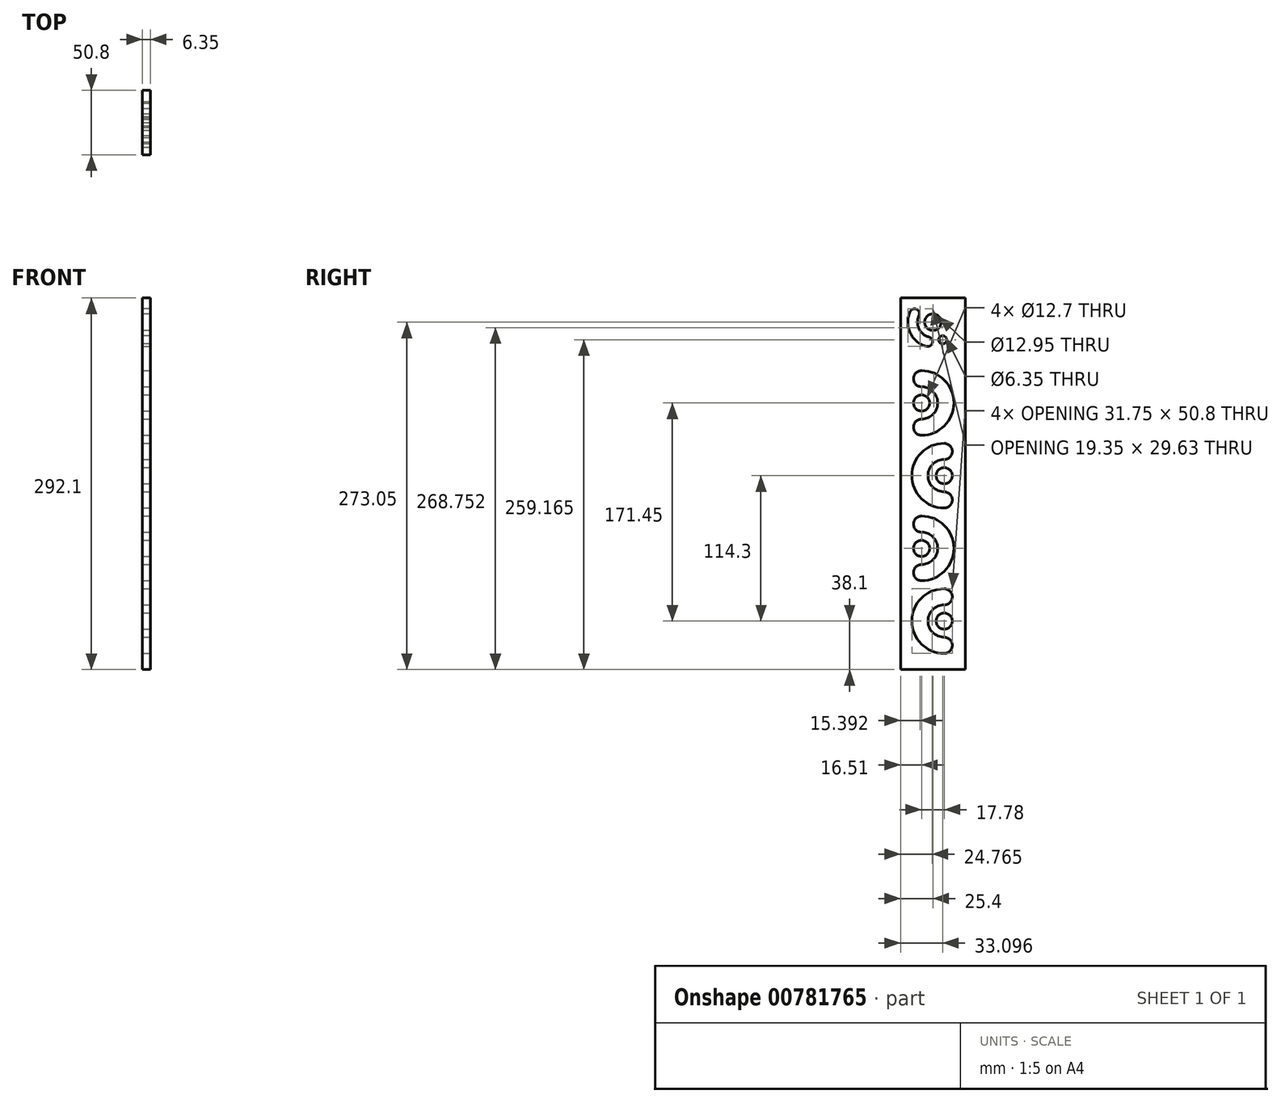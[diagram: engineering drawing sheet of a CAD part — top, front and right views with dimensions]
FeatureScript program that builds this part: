
annotation { "Feature Type Name" : "Feature", "Feature Type Description" : "" }
export const myFeature = defineFeature(function(context is Context, id is Id, definition is map)
    precondition{}
    {
        {
            var Q0;
            Q0=qCreatedBy(makeId("Top.planeOp"),FACE);
            var sketch = newSketch(context, id + "F0", { "sketchPlane" : qUnion([Q0])});
            skLineSegment(sketch, "E0.bottom", {"start": v(31.75, -31.75) * mm, "end": v(-31.75, -31.75) * mm});
            skLineSegment(sketch, "E0.top", {"start": v(31.75, 31.75) * mm, "end": v(-31.75, 31.75) * mm});
            skLineSegment(sketch, "E0.left", {"start": v(31.75, -31.75) * mm, "end": v(31.75, 31.75) * mm});
            skLineSegment(sketch, "E0.right", {"start": v(-31.75, -31.75) * mm, "end": v(-31.75, 31.75) * mm});
            skPoint(sketch, "E0.middle", {"position": v(0, 0) * mm});
            skLineSegment(sketch, "E1.bottom", {"start": v(25.4, -25.4) * mm, "end": v(-25.4, -25.4) * mm});
            skLineSegment(sketch, "E1.top", {"start": v(25.4, 25.4) * mm, "end": v(-25.4, 25.4) * mm});
            skLineSegment(sketch, "E1.left", {"start": v(25.4, -25.4) * mm, "end": v(25.4, 25.4) * mm});
            skLineSegment(sketch, "E1.right", {"start": v(-25.4, -25.4) * mm, "end": v(-25.4, 25.4) * mm});
            skSolve(sketch);
        }
        {
            var Q0;
            Q0=makeQuery(id+"F0.imprint","IMPRINT",FACE,{"disambiguationData":[TD([[makeQuery(id+"F0.imprint","IMPRINT",EDGE,{"derivedFrom":sQuery(id+"F0.wireOp",EDGE,"E0.bottom")}),-1.0]])]});
            extrude(context, id + "F1", {"entities" : qUnion([Q0]), "endBound" : BoundingType.SYMMETRIC, "depth" : 330.2 * mm, "offsetDistance" : 25.4 * mm});
        }
        {
            var Q0;
            Q0=makeQuery(id+"F1.opExtrude","SWEPT_FACE",FACE,{"disambiguationData":[OSD([sQuery(id+"F0.wireOp",EDGE,"E0.right")])]});
            var sketch = newSketch(context, id + "F2", { "sketchPlane" : qUnion([Q0])});
            skSolve(sketch);
        }
        {
            var Q0;
            Q0=makeQuery(id+"F1.opExtrude","SWEPT_FACE",FACE,{"disambiguationData":[OSD([sQuery(id+"F0.wireOp",EDGE,"E0.left")])]});
            var sketch = newSketch(context, id + "F3", { "sketchPlane" : qUnion([Q0])});
            skLineSegment(sketch, "E2.0", {"start": v(-31.75, 165.1) * mm, "end": v(31.75, 165.1) * mm, "construction": true});
            skLineSegment(sketch, "E2.1", {"start": v(-31.75, 165.1) * mm, "end": v(-31.75, -165.1) * mm, "construction": true});
            skLineSegment(sketch, "E2.2", {"start": v(31.75, 165.1) * mm, "end": v(31.75, -165.1) * mm, "construction": true});
            skLineSegment(sketch, "E2.3", {"start": v(-31.75, -165.1) * mm, "end": v(31.75, -165.1) * mm, "construction": true});
            skCircle(sketch, "E3", {"center": v(0, 146.05) * mm, "radius": 6.48 * mm});
            skArc(sketch, "E4", {"start": v(17.84, 137.73) * mm, "mid": v(19.5, 143.31) * mm, "end": v(19.44, 149.13) * mm});
            skArc(sketch, "E5", {"start": v(10.93, 140.95) * mm, "mid": v(11.95, 144.37) * mm, "end": v(11.92, 147.94) * mm});
            skLineSegment(sketch, "E6", {"start": v(0, 146.05) * mm, "end": v(19.44, 149.13) * mm, "construction": true});
            skLineSegment(sketch, "E7", {"start": v(0, 146.05) * mm, "end": v(9.54, 128.83) * mm, "construction": true});
            skLineSegment(sketch, "E8", {"start": v(0, 146.05) * mm, "end": v(24.19, 134.77) * mm, "construction": true});
            skCircle(sketch, "E9", {"center": v(0, 146.05) * mm, "radius": 15.88 * mm, "construction": true});
            skArc(sketch, "E10", {"start": v(11.92, 147.94) * mm, "mid": v(15.08, 152.3) * mm, "end": v(19.44, 149.13) * mm});
            skArc(sketch, "E11.MirrorCS", {"start": v(6.21, 135.7) * mm, "mid": v(4.91, 130.48) * mm, "end": v(10.14, 129.18) * mm});
            skArc(sketch, "E12.MirrorCS", {"start": v(10.93, 140.95) * mm, "mid": v(8.97, 137.98) * mm, "end": v(6.21, 135.7) * mm});
            skArc(sketch, "E13.MirrorCS", {"start": v(17.84, 137.73) * mm, "mid": v(14.63, 132.88) * mm, "end": v(10.14, 129.18) * mm});
            skLineSegment(sketch, "E14", {"start": v(0, 146.05) * mm, "end": v(-19.11, 146.05) * mm, "construction": true});
            skLineSegment(sketch, "E15", {"start": v(0, 146.05) * mm, "end": v(0, 119.4) * mm, "construction": true});
            skArc(sketch, "E16.MirrorCS", {"start": v(-6.21, 135.7) * mm, "mid": v(-4.91, 130.48) * mm, "end": v(-10.14, 129.18) * mm});
            skArc(sketch, "E17.MirrorCS", {"start": v(-17.84, 137.73) * mm, "mid": v(-14.63, 132.88) * mm, "end": v(-10.14, 129.18) * mm});
            skArc(sketch, "E18.MirrorCS", {"start": v(-17.84, 137.73) * mm, "mid": v(-19.5, 143.31) * mm, "end": v(-19.44, 149.13) * mm});
            skArc(sketch, "E19.MirrorCS", {"start": v(-11.92, 147.94) * mm, "mid": v(-15.08, 152.3) * mm, "end": v(-19.44, 149.13) * mm});
            skArc(sketch, "E20.MirrorCS", {"start": v(-10.93, 140.95) * mm, "mid": v(-11.95, 144.37) * mm, "end": v(-11.92, 147.94) * mm});
            skArc(sketch, "E21.MirrorCS", {"start": v(-10.93, 140.95) * mm, "mid": v(-8.97, 137.98) * mm, "end": v(-6.21, 135.7) * mm});
            skSolve(sketch);
        }
        {
            var Q0;
            Q0=makeQuery(id+"F3.imprint","IMPRINT",FACE,{"disambiguationData":[TD([[makeQuery(id+"F3.imprint","IMPRINT",EDGE,{"derivedFrom":sQuery(id+"F3.wireOp",EDGE,"E3")}),1.0]])]});
            var Q1;
            Q1=makeQuery(id+"F3.imprint","IMPRINT",FACE,{"disambiguationData":[TD([[makeQuery(id+"F3.imprint","IMPRINT",EDGE,{"derivedFrom":sQuery(id+"F3.wireOp",EDGE,"E4")}),1.0]])]});
            var Q2;
            Q2=makeQuery(id+"F3.imprint","IMPRINT",FACE,{"disambiguationData":[TD([[makeQuery(id+"F3.imprint","IMPRINT",EDGE,{"derivedFrom":sQuery(id+"F3.wireOp",EDGE,"E16.MirrorCS")}),-1.0]])]});
            extrude(context, id + "F4", {"entities" : qUnion([Q0, Q1, Q2]), "operationType" : NewBodyOperationType.REMOVE, "oppositeDirection" : true, "depth" : 25.4 * mm, "offsetDistance" : 25.4 * mm});
        }
        {
            var Q0;
            {var subQ0=sQuery(id+"F0.wireOp",EDGE,"E0.right");Q0=makeQuery(id+"F2.imprint","IMPRINT",FACE,{"disambiguationData":[TD([[makeQuery(id+"F2.imprint","IMPRINT",EDGE,{"derivedFrom":makeQuery(id+"F1.opExtrude","CAP_EDGE",EDGE,{"disambiguationData":[OSD([subQ0])],"isStart":true})}),-1.0]])]});}
            var sketch = newSketch(context, id + "F5", { "sketchPlane" : qUnion([Q0])});
            skCircle(sketch, "E22", {"center": v(0, 146.05) * mm, "radius": 6.48 * mm});
            skCircle(sketch, "E23", {"center": v(-7.7, 132.17) * mm, "radius": 3.18 * mm});
            skArc(sketch, "E24", {"start": v(5.1, 127.04) * mm, "mid": v(17.84, 137.73) * mm, "end": v(17.84, 154.37) * mm});
            skCircle(sketch, "E25", {"center": v(0, 146.05) * mm, "radius": 15.88 * mm, "construction": true});
            skLineSegment(sketch, "E26", {"start": v(0, 146.05) * mm, "end": v(5.1, 127.04) * mm, "construction": true});
            skLineSegment(sketch, "E27", {"start": v(0, 146.05) * mm, "end": v(-15.88, 146.05) * mm, "construction": true});
            skLineSegment(sketch, "E28", {"start": v(0, 146.05) * mm, "end": v(17.84, 154.37) * mm, "construction": true});
            skArc(sketch, "E29", {"start": v(3.12, 134.4) * mm, "mid": v(10.93, 140.95) * mm, "end": v(10.93, 151.15) * mm});
            skLineSegment(sketch, "E30", {"start": v(0, 146.05) * mm, "end": v(-7.7, 132.17) * mm});
            skArc(sketch, "E31", {"start": v(3.12, 134.4) * mm, "mid": v(0.43, 129.73) * mm, "end": v(5.1, 127.04) * mm});
            skArc(sketch, "E32", {"start": v(17.84, 154.37) * mm, "mid": v(12.78, 156.21) * mm, "end": v(10.93, 151.15) * mm});
            skCircle(sketch, "E33", {"center": v(-7.7, 132.17) * mm, "radius": 1.59 * mm, "construction": true});
            skLineSegment(sketch, "E34", {"start": v(0, 146.05) * mm, "end": v(-15.58, 149.08) * mm, "construction": true});
            skCircle(sketch, "E35", {"center": v(-15.58, 149.08) * mm, "radius": 3.18 * mm, "construction": true});
            skArc(sketch, "E36.0", {"start": v(-11.92, 147.94) * mm, "mid": v(-15.08, 152.3) * mm, "end": v(-19.44, 149.13) * mm, "construction": true});
            skLineSegment(sketch, "E37", {"start": v(0, 146.05) * mm, "end": v(-15.68, 148.53) * mm, "construction": true});
            skSolve(sketch);
        }
        {
            var Q0;
            Q0=qSketchRegion(id+"F5",true);
            extrude(context, id + "F6", {"entities" : qUnion([Q0]), "operationType" : NewBodyOperationType.REMOVE, "oppositeDirection" : true, "depth" : 25.4 * mm, "offsetDistance" : 25.4 * mm});
        }
        {
            var Q0;
            Q0=makeQuery(id+"F1.opExtrude","SWEPT_FACE",FACE,{"disambiguationData":[OSD([sQuery(id+"F0.wireOp",EDGE,"E0.left")])]});
            var sketch = newSketch(context, id + "F7", { "sketchPlane" : qUnion([Q0])});
            skArc(sketch, "E38", {"start": v(-8.89, 101.6) * mm, "mid": v(10.16, 82.55) * mm, "end": v(-8.89, 63.5) * mm, "construction": true});
            skArc(sketch, "E39.0", {"start": v(-8.89, 95.25) * mm, "mid": v(3.81, 82.55) * mm, "end": v(-8.89, 69.85) * mm});
            skArc(sketch, "E40.0", {"start": v(-8.89, 107.95) * mm, "mid": v(16.5, 82.55) * mm, "end": v(-8.89, 57.15) * mm});
            skArc(sketch, "E41", {"start": v(-8.89, 107.95) * mm, "mid": v(-15.24, 101.6) * mm, "end": v(-8.89, 95.25) * mm});
            skArc(sketch, "E42", {"start": v(-8.89, 57.15) * mm, "mid": v(-15.24, 63.5) * mm, "end": v(-8.89, 69.85) * mm});
            skArc(sketch, "E43", {"start": v(8.9, 6.35) * mm, "mid": v(-10.16, 25.4) * mm, "end": v(8.9, 44.45) * mm, "construction": true});
            skArc(sketch, "E44.0", {"start": v(8.9, 12.7) * mm, "mid": v(-3.8, 25.4) * mm, "end": v(8.9, 38.1) * mm});
            skArc(sketch, "E45.0", {"start": v(8.9, 0) * mm, "mid": v(-16.5, 25.4) * mm, "end": v(8.89, 50.8) * mm});
            skArc(sketch, "E46", {"start": v(8.9, 0) * mm, "mid": v(15.24, 6.35) * mm, "end": v(8.9, 12.7) * mm});
            skArc(sketch, "E47", {"start": v(8.9, 50.8) * mm, "mid": v(15.24, 44.45) * mm, "end": v(8.9, 38.1) * mm});
            skArc(sketch, "E48", {"start": v(-8.89, -12.7) * mm, "mid": v(10.16, -31.75) * mm, "end": v(-8.89, -50.8) * mm, "construction": true});
            skArc(sketch, "E49.0", {"start": v(-8.89, -19.05) * mm, "mid": v(3.81, -31.75) * mm, "end": v(-8.89, -44.45) * mm});
            skArc(sketch, "E50.0", {"start": v(-8.89, -6.35) * mm, "mid": v(16.5, -31.75) * mm, "end": v(-8.89, -57.15) * mm});
            skArc(sketch, "E51", {"start": v(-8.89, -6.35) * mm, "mid": v(-15.24, -12.7) * mm, "end": v(-8.89, -19.05) * mm});
            skArc(sketch, "E52", {"start": v(-8.89, -57.15) * mm, "mid": v(-15.24, -50.8) * mm, "end": v(-8.89, -44.45) * mm});
            skArc(sketch, "E53", {"start": v(8.9, -107.95) * mm, "mid": v(-10.16, -88.9) * mm, "end": v(8.89, -69.85) * mm, "construction": true});
            skArc(sketch, "E54.0", {"start": v(8.9, -101.6) * mm, "mid": v(-3.8, -88.9) * mm, "end": v(8.89, -76.2) * mm});
            skArc(sketch, "E55.0", {"start": v(8.9, -114.3) * mm, "mid": v(-16.5, -88.9) * mm, "end": v(8.89, -63.5) * mm});
            skArc(sketch, "E56", {"start": v(8.9, -114.3) * mm, "mid": v(15.24, -107.95) * mm, "end": v(8.9, -101.6) * mm});
            skArc(sketch, "E57", {"start": v(8.89, -63.5) * mm, "mid": v(15.24, -69.85) * mm, "end": v(8.89, -76.2) * mm});
            skCircle(sketch, "E58", {"center": v(-8.89, 82.55) * mm, "radius": 6.35 * mm});
            skCircle(sketch, "E59", {"center": v(8.9, 25.4) * mm, "radius": 6.35 * mm});
            skCircle(sketch, "E60", {"center": v(8.9, -88.9) * mm, "radius": 6.35 * mm});
            skCircle(sketch, "E61", {"center": v(-8.89, -31.75) * mm, "radius": 6.35 * mm});
            skSolve(sketch);
        }
        {
            var Q0;
            Q0=qSketchRegion(id+"F7",true);
            extrude(context, id + "F8", {"entities" : qUnion([Q0]), "operationType" : NewBodyOperationType.REMOVE, "endBound" : BoundingType.THROUGH_ALL, "oppositeDirection" : true, "depth" : 25.4 * mm, "offsetDistance" : 25.4 * mm});
        }
        {
            var Q0;
            Q0=makeQuery(id+"F1.opExtrude","SWEPT_FACE",FACE,{"disambiguationData":[OSD([sQuery(id+"F0.wireOp",EDGE,"E1.left")])]});
            var sketch = newSketch(context, id + "F9", { "sketchPlane" : qUnion([Q0])});
            skLineSegment(sketch, "E62.bottom", {"start": v(-25.4, 165.1) * mm, "end": v(25.4, 165.1) * mm});
            skLineSegment(sketch, "E62.top", {"start": v(-25.4, -127) * mm, "end": v(25.4, -127) * mm});
            skLineSegment(sketch, "E62.left", {"start": v(-25.4, 165.1) * mm, "end": v(-25.4, -127) * mm});
            skLineSegment(sketch, "E62.right", {"start": v(25.4, 165.1) * mm, "end": v(25.4, -127) * mm});
            skLineSegment(sketch, "E63.bottom", {"start": v(72.9, -188.97) * mm, "end": v(-72.9, -188.97) * mm});
            skLineSegment(sketch, "E63.top", {"start": v(72.9, 188.97) * mm, "end": v(-72.9, 188.97) * mm});
            skLineSegment(sketch, "E63.left", {"start": v(72.9, -188.97) * mm, "end": v(72.9, 188.97) * mm});
            skLineSegment(sketch, "E63.right", {"start": v(-72.9, -188.97) * mm, "end": v(-72.9, 188.97) * mm});
            skPoint(sketch, "E63.middle", {"position": v(0, 0) * mm});
            skSolve(sketch);
        }
        {
            var Q0;
            Q0 = qSketchRegion(id + "F9", true);
            extrude(context, id + "F10", {"entities" : qUnion([Q0]), "operationType" : NewBodyOperationType.REMOVE, "endBound" : BoundingType.SYMMETRIC, "oppositeDirection" : true, "depth" : 127 * mm, "offsetDistance" : 25.4 * mm});
        }
        {
            var Q0;
            Q0=makeQuery(id+"F1.opExtrude","SWEPT_FACE",FACE,{"disambiguationData":[OSD([sQuery(id+"F0.wireOp",EDGE,"E1.right")])]});
            var sketch = newSketch(context, id + "F11", { "sketchPlane" : qUnion([Q0])});
            skLineSegment(sketch, "E64.bottom", {"start": v(-48.84, -169.45) * mm, "end": v(48.84, -169.45) * mm});
            skLineSegment(sketch, "E64.top", {"start": v(-48.84, 169.45) * mm, "end": v(48.84, 169.45) * mm});
            skLineSegment(sketch, "E64.left", {"start": v(-48.84, -169.45) * mm, "end": v(-48.84, 169.45) * mm});
            skLineSegment(sketch, "E64.right", {"start": v(48.84, -169.45) * mm, "end": v(48.84, 169.45) * mm});
            skPoint(sketch, "E64.middle", {"position": v(0, 0) * mm});
            skSolve(sketch);
        }
        {
            var Q0;
            Q0 = qSketchRegion(id + "F11", true);
            extrude(context, id + "F12", {"entities" : qUnion([Q0]), "operationType" : NewBodyOperationType.REMOVE, "endBound" : BoundingType.THROUGH_ALL, "depth" : 25.4 * mm, "offsetDistance" : 25.4 * mm});
        }
    });
